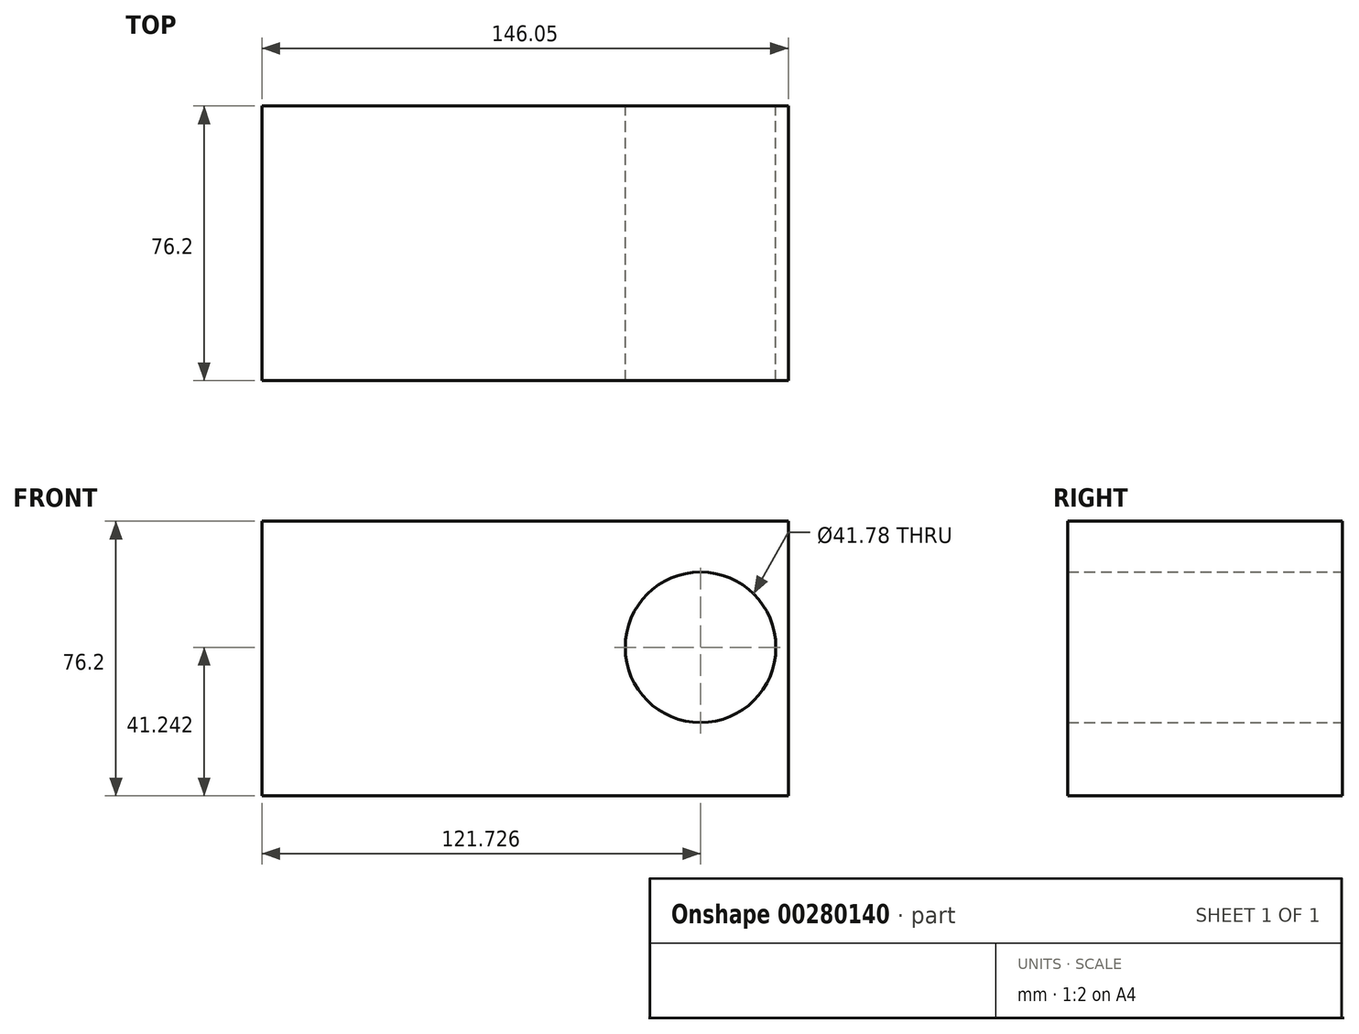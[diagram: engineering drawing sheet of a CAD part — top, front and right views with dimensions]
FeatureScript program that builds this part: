
annotation { "Feature Type Name" : "Feature", "Feature Type Description" : "" }
export const myFeature = defineFeature(function(context is Context, id is Id, definition is map)
    precondition{}
    {
        {
            var Q0;
            Q0=qCreatedBy(makeId("Front.planeOp"),FACE);
            var sketch = newSketch(context, id + "F0", { "sketchPlane" : qUnion([Q0])});
            skLineSegment(sketch, "E0.bottom", {"start": v(-93.54, 51.38) * mm, "end": v(52.51, 51.38) * mm});
            skLineSegment(sketch, "E0.top", {"start": v(-93.54, -24.82) * mm, "end": v(52.51, -24.82) * mm});
            skLineSegment(sketch, "E0.left", {"start": v(-93.54, 51.38) * mm, "end": v(-93.54, -24.82) * mm});
            skLineSegment(sketch, "E0.right", {"start": v(52.51, 51.38) * mm, "end": v(52.51, -24.82) * mm});
            skSolve(sketch);
        }
        {
            var Q0;
            Q0=makeQuery(id+"F0.imprint","IMPRINT",FACE,{"disambiguationData":[TD([[makeQuery(id+"F0.imprint","IMPRINT",EDGE,{"derivedFrom":sQuery(id+"F0.wireOp",EDGE,"E0.bottom")}),-1.0]])]});
            var sketch = newSketch(context, id + "F1", { "sketchPlane" : qUnion([Q0])});
            skLineSegment(sketch, "E1.bottom", {"start": v(-65, 25.4) * mm, "end": v(-39.6, 25.4) * mm});
            skLineSegment(sketch, "E1.top", {"start": v(-65, 0) * mm, "end": v(-39.6, 0) * mm});
            skLineSegment(sketch, "E1.left", {"start": v(-65, 25.4) * mm, "end": v(-65, 0) * mm});
            skLineSegment(sketch, "E1.right", {"start": v(-39.6, 25.4) * mm, "end": v(-39.6, 0) * mm});
            skSolve(sketch);
        }
        {
            var Q0;
            Q0 = qSketchRegion(id + "F0", true);
            extrude(context, id + "F2", {"entities" : qUnion([Q0]), "depth" : 76.2 * mm});
        }
        {
            var Q0;
            Q0=makeQuery(id+"F1.imprint","IMPRINT",FACE,{"disambiguationData":[TD([[makeQuery(id+"F1.imprint","IMPRINT",EDGE,{"derivedFrom":sQuery(id+"F1.wireOp",EDGE,"E1.bottom")}),1.0]])]});
            var sketch = newSketch(context, id + "F3", { "sketchPlane" : qUnion([Q0])});
            skCircle(sketch, "E2", {"center": v(28.19, 16.42) * mm, "radius": 20.89 * mm});
            skSolve(sketch);
        }
        {
            var Q0;
            Q0 = qSketchRegion(id + "F3", true);
            extrude(context, id + "F4", {"entities" : qUnion([Q0]), "operationType" : NewBodyOperationType.REMOVE, "depth" : 76.2 * mm});
        }
        {
            var Q0;
            Q0=makeQuery(id+"F1.imprint","IMPRINT",FACE,{"disambiguationData":[TD([[makeQuery(id+"F1.imprint","IMPRINT",EDGE,{"derivedFrom":sQuery(id+"F1.wireOp",EDGE,"E1.bottom")}),-1.0]])]});
            extrude(context, id + "F5", {"entities" : qUnion([Q0]), "operationType" : NewBodyOperationType.ADD, "depth" : 76.2 * mm});
        }
    });
